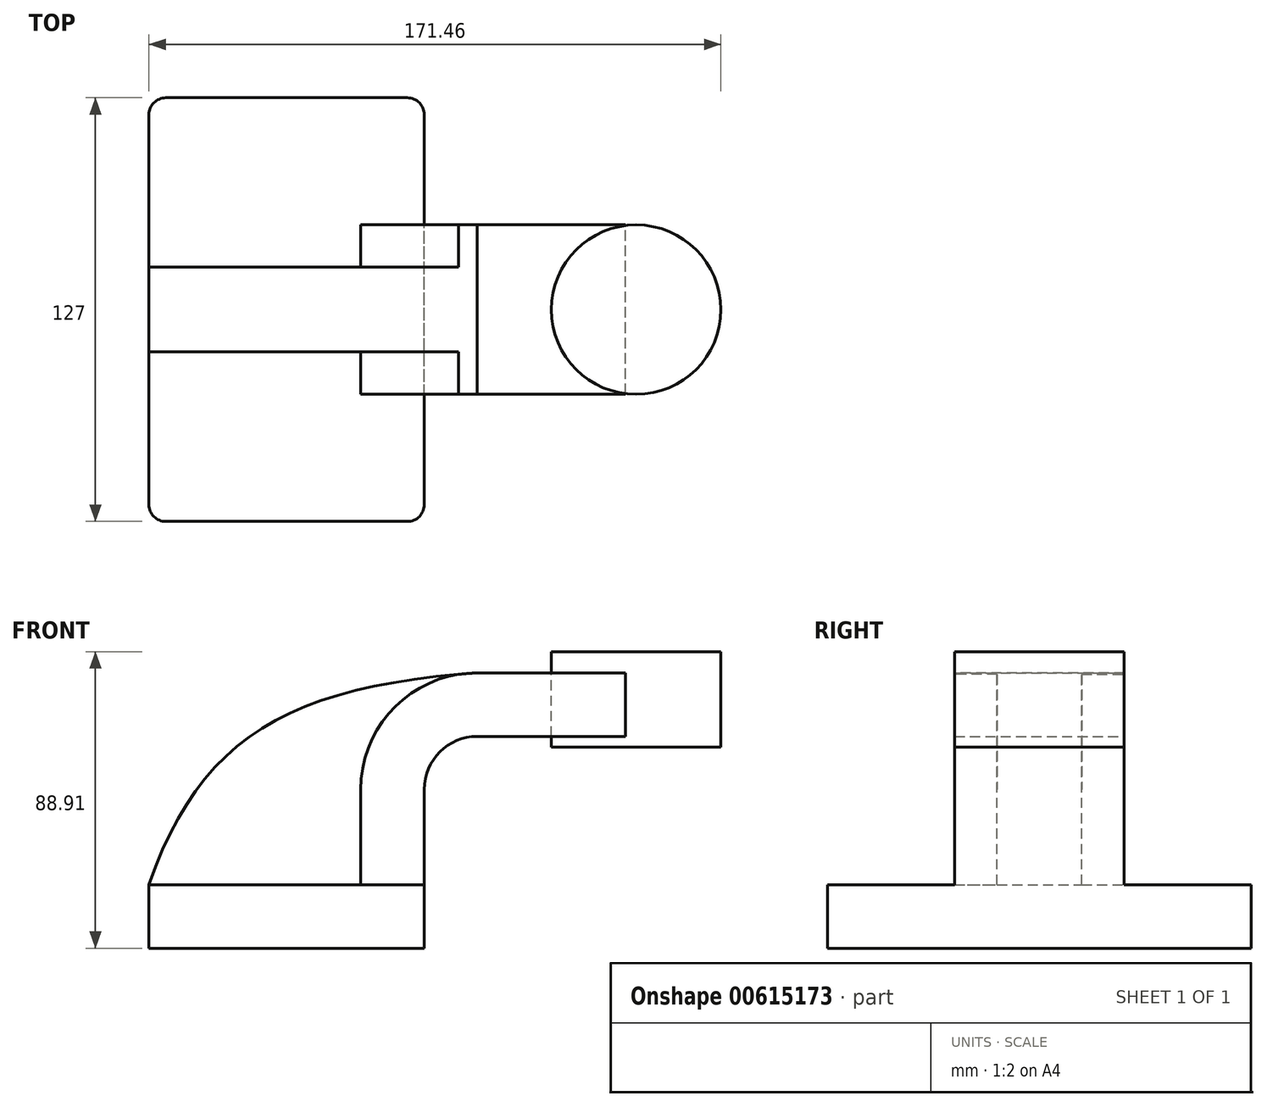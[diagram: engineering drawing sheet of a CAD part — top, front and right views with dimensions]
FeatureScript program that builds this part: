
annotation { "Feature Type Name" : "Feature", "Feature Type Description" : "" }
export const myFeature = defineFeature(function(context is Context, id is Id, definition is map)
    precondition{}
    {
        {
            var Q0;
            Q0=qCreatedBy(makeId("Front.planeOp"),FACE);
            var sketch = newSketch(context, id + "F0", { "sketchPlane" : qUnion([Q0])});
            skLineSegment(sketch, "E0.bottom", {"start": v(-41.28, 9.52) * mm, "end": v(41.27, 9.53) * mm});
            skLineSegment(sketch, "E0.top", {"start": v(-41.28, -9.53) * mm, "end": v(41.28, -9.53) * mm});
            skLineSegment(sketch, "E0.left", {"start": v(-41.28, 9.52) * mm, "end": v(-41.27, -9.53) * mm});
            skLineSegment(sketch, "E0.right", {"start": v(41.28, 9.53) * mm, "end": v(41.28, -9.52) * mm});
            skPoint(sketch, "E0.middle", {"position": v(0, 0) * mm});
            skLineSegment(sketch, "E1.bottom", {"start": v(79.37, 79.38) * mm, "end": v(130.17, 79.38) * mm});
            skLineSegment(sketch, "E1.top", {"start": v(79.38, 50.8) * mm, "end": v(130.17, 50.8) * mm});
            skLineSegment(sketch, "E1.left", {"start": v(79.37, 79.38) * mm, "end": v(79.37, 50.8) * mm});
            skLineSegment(sketch, "E1.right", {"start": v(130.17, 79.38) * mm, "end": v(130.17, 50.8) * mm});
            skPoint(sketch, "E1.middle", {"position": v(104.77, 65.09) * mm});
            skLineSegment(sketch, "E2", {"start": v(41.27, 9.53) * mm, "end": v(41.27, 38.1) * mm});
            skArc(sketch, "E3", {"start": v(41.27, 38.1) * mm, "mid": v(45.92, 49.33) * mm, "end": v(57.15, 53.98) * mm});
            skLineSegment(sketch, "E4", {"start": v(57.15, 53.98) * mm, "end": v(101.6, 53.98) * mm});
            skLineSegment(sketch, "E5.0", {"start": v(57.15, 73.03) * mm, "end": v(101.6, 73.03) * mm});
            skArc(sketch, "E5.1", {"start": v(22.22, 38.1) * mm, "mid": v(32.45, 62.8) * mm, "end": v(57.15, 73.03) * mm});
            skLineSegment(sketch, "E5.2", {"start": v(22.22, 9.53) * mm, "end": v(22.22, 38.1) * mm});
            skFitSpline(sketch, "E6", {"points": [v(-41.28, 9.52) * mm, v(57.15, 73.03) * mm], "startDerivative": vector(45.6, 131.14) * mm, "endDerivative": vector(171.45, 12.37) * mm});
            skLineSegment(sketch, "E7", {"start": v(101.6, 73.03) * mm, "end": v(101.6, 53.98) * mm});
            skLineSegment(sketch, "E8", {"start": v(104.77, 65.09) * mm, "end": v(104.77, 79.38) * mm});
            skLineSegment(sketch, "E9", {"start": v(104.77, 65.09) * mm, "end": v(104.77, 50.8) * mm});
            skSolve(sketch);
        }
        {
            var Q0;
            Q0=makeQuery(id+"F0.imprint","IMPRINT",FACE,{"disambiguationData":[TD([[makeQuery(id+"F0.imprint","IMPRINT",EDGE,{"derivedFrom":sQuery(id+"F0.wireOp",EDGE,"E0.top")}),1.0]])]});
            extrude(context, id + "F1", {"entities" : qUnion([Q0]), "endBound" : BoundingType.SYMMETRIC, "depth" : 127 * mm, "offsetDistance" : 25.4 * mm});
        }
        {
            var Q0;
            {var subQ1=sQuery(id+"F0.wireOp",EDGE,"E2");Q0=makeQuery(id+"F0.imprint","IMPRINT",FACE,{"disambiguationData":[TD([[makeQuery(id+"F0.imprint","IMPRINT",EDGE,{"derivedFrom":subQ1}),1.0]])]});}
            var Q1;
            {var subQ5=sQuery(id+"F0.wireOp",EDGE,"E7");Q1=makeQuery(id+"F0.imprint","IMPRINT",FACE,{"disambiguationData":[TD([[makeQuery(id+"F0.imprint","IMPRINT",EDGE,{"derivedFrom":subQ5}),-1.0]])]});}
            extrude(context, id + "F2", {"entities" : qUnion([Q0, Q1]), "operationType" : NewBodyOperationType.ADD, "endBound" : BoundingType.SYMMETRIC, "depth" : 50.8 * mm, "offsetDistance" : 25.4 * mm});
        }
        {
            var Q0;
            {var subQ3=sQuery(id+"F0.wireOp",EDGE,"E5.2");Q0=makeQuery(id+"F0.imprint","IMPRINT",FACE,{"disambiguationData":[TD([[makeQuery(id+"F0.imprint","IMPRINT",EDGE,{"derivedFrom":subQ3}),1.0]])]});}
            extrude(context, id + "F3", {"entities" : qUnion([Q0]), "operationType" : NewBodyOperationType.ADD, "endBound" : BoundingType.SYMMETRIC, "depth" : 25.4 * mm, "offsetDistance" : 25.4 * mm});
        }
        {
            var Q0;
            {var subQ4=sQuery(id+"F0.wireOp",EDGE,"E1.bottom");Q0=makeQuery(id+"F0.imprint","IMPRINT",FACE,{"disambiguationData":[TD([[makeQuery(id+"F0.imprint","IMPRINT",EDGE,{"derivedFrom":subQ4}),-1.0]])]});}
            var Q1;
            Q1=sQuery(id+"F0.wireOp",EDGE,"E9");
            revolve(context, id + "F4", {"entities" : qUnion([Q0]), "axis" : qUnion([Q1]), "revolveType" : RevolveType.FULL});
        }
        {
            var Q0;
            Q0=makeQuery(id+"F1.opExtrude","CAP_EDGE",EDGE,{"disambiguationData":[OSD([sQuery(id+"F0.wireOp",EDGE,"E0.left")])],"isStart":false});
            var Q1;
            Q1=makeQuery(id+"F1.opExtrude","CAP_EDGE",EDGE,{"disambiguationData":[OSD([sQuery(id+"F0.wireOp",EDGE,"E0.right")])],"isStart":false});
            var Q2;
            Q2=makeQuery(id+"F1.opExtrude","CAP_EDGE",EDGE,{"disambiguationData":[OSD([sQuery(id+"F0.wireOp",EDGE,"E0.right")])],"isStart":true});
            var Q3;
            Q3=makeQuery(id+"F1.opExtrude","CAP_EDGE",EDGE,{"disambiguationData":[OSD([sQuery(id+"F0.wireOp",EDGE,"E0.left")])],"isStart":true});
            fillet(context, id + "F5", {"entities" : qUnion([Q0, Q1, Q2, Q3]), "radius" : 5.08 * mm, "tangentPropagation" : true, "allowEdgeOverflow" : false});
        }
    });
